# Revit family: DOT BLOCK CEILLING 946_DTSM40N9.1.15
name_source: partatom
category: Luminarias
units: mm (PartAtom-declared; Revit-internal decimal feet)

## family parameters
Compartido = No
Corte con vacíos al cargar = No
Cota de conector redondo = Diámetro de uso
Origen de luz = Sí
Punto de cálculo de habitación = No
Se basa en plano de trabajo = Sí
Siempre vertical = Sí
Tipo de pieza = Normal

## types (1)
- DOT BLOCK CEILLING 946_DTSM40N9.1.15
    Archivo de red fotométrica = L964A-40W-840-B-15_IESNA95.IES
    Cambio de temperatura de color de luz atenuada = <Ninguno>
    Comentarios de vataje = 90-240V
    Descripción = LUMINARIA DOWNLIGHT EN FORMATO RECTANGULAR PARA SOBREPONER DIRECTO EN TECHO, CUERPO DE ALUMINIO ACABADO EN COLOR NEGRO, IP 20, PESO 1.98Kg, TIPO DE LED 3030SMD PHILIPS CON 40W TOTAL, 3200 LUMENES, 82LM/W, IRC 90, TEMPERATURA EN BLANCO FRIO 4000K, 50 MIL HORAS DE VIDA PROMEDIO, APERTURA DE 15 GRADOS POR PROYECTO, ALIMENTADO A 90-240V
    Elevación por defecto = 1219 mm
    Fabricante = BRILLANT
    Filtro de color = 16777215
    Lámpara = 3030SMD PHILIPS
    Modelo = DTSM40N9.1.15
    Watt per fixture = 40
    Ángulo de inclinación = 60.00°

## geometry (parser evidence)
native form markers: Blend x2
no freeform markers — native parametric forms only
